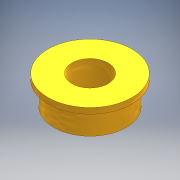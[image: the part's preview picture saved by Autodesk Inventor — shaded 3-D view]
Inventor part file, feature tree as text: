
AUTODESK INVENTOR PART (.ipt)
format: ipt  version: 2020.2 (Build 242310000, 310)  size: 107,520 bytes
history: native  units: mm
features: extrude x2, other x1, sketch x1
ambient origin geometry x8: Origin, YZ Plane, XZ Plane, XY Plane, X Axis, Y Axis, Z Axis, Center Point
bodies: Body1 (feature_tree)
feature tree (4):
  other  "ソリッド1"
  sketch  "スケッチ1"
  extrude  "押し出し1"  Depth=5.0mm
  extrude  "押し出し2"  Depth=10.0mm
